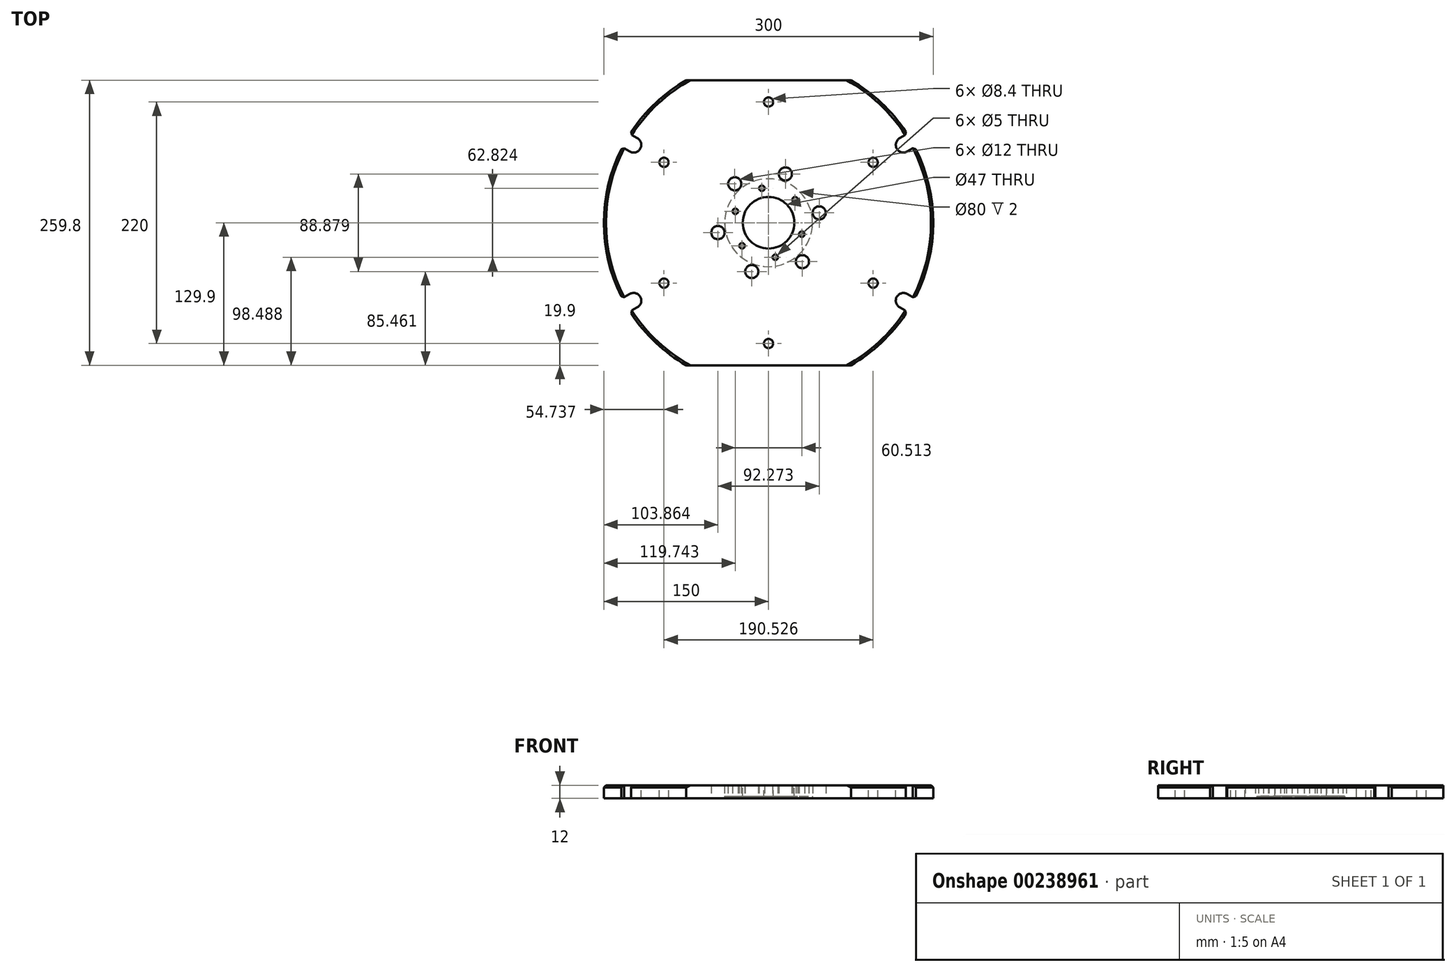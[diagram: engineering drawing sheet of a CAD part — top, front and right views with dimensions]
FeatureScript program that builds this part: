
annotation { "Feature Type Name" : "Feature", "Feature Type Description" : "" }
export const myFeature = defineFeature(function(context is Context, id is Id, definition is map)
    precondition{}
    {
        {
            var Q0;
            Q0=qCreatedBy(makeId("Top.planeOp"),FACE);
            var sketch = newSketch(context, id + "F0", { "sketchPlane" : qUnion([Q0])});
            skArc(sketch, "E0.cCircle", {"start": v(-75, 129.9) * mm, "mid": v(-103.56, 108.51) * mm, "end": v(-126.26, 80.98) * mm});
            skLineSegment(sketch, "E0.1", {"start": v(-75, 129.9) * mm, "end": v(75, 129.9) * mm});
            skLineSegment(sketch, "E0.4", {"start": v(75, -129.9) * mm, "end": v(-75, -129.9) * mm});
            skPoint(sketch, "E0.5.end.orphan", {"position": v(-150, 0) * mm});
            skCircle(sketch, "E1", {"center": v(0, 0) * mm, "radius": 110 * mm, "construction": true});
            skCircle(sketch, "E2", {"center": v(0, 110) * mm, "radius": 4.2 * mm});
            skCircle(sketch, "E3.1.0", {"center": v(-95.26, 55) * mm, "radius": 4.2 * mm});
            skCircle(sketch, "E3.2.0", {"center": v(-95.26, -55) * mm, "radius": 4.2 * mm});
            skCircle(sketch, "E3.3.0", {"center": v(0, -110) * mm, "radius": 4.2 * mm});
            skCircle(sketch, "E3.4.0", {"center": v(95.26, -55) * mm, "radius": 4.2 * mm});
            skCircle(sketch, "E3.5.0", {"center": v(95.26, 55) * mm, "radius": 4.2 * mm});
            skCircle(sketch, "E4", {"center": v(0, 0) * mm, "radius": 23.5 * mm});
            skLineSegment(sketch, "E5", {"start": v(-75, 129.9) * mm, "end": v(-150, 0) * mm, "construction": true});
            skLineSegment(sketch, "E6", {"start": v(0, 0) * mm, "end": v(-148.53, 85.75) * mm, "construction": true});
            skLineSegment(sketch, "E7", {"start": v(-110.04, 93.22) * mm, "end": v(-133.2, 53.1) * mm, "construction": true});
            skArc(sketch, "E8", {"start": v(-126.4, 64.89) * mm, "mid": v(-116.83, 67.45) * mm, "end": v(-119.4, 77.01) * mm});
            skLineSegment(sketch, "E9", {"start": v(-119.4, 77.01) * mm, "end": v(-126.26, 80.98) * mm});
            skLineSegment(sketch, "E10.MirrorCS", {"start": v(-126.4, 64.89) * mm, "end": v(-133.26, 68.86) * mm});
            skArc(sketch, "E11.trimOffspring", {"start": v(-133.26, 68.86) * mm, "mid": v(-145.76, 35.43) * mm, "end": v(-150, 0) * mm});
            skLineSegment(sketch, "E12", {"start": v(0, 0) * mm, "end": v(-185.74, 0) * mm, "construction": true});
            skLineSegment(sketch, "E13", {"start": v(0, -5.52) * mm, "end": v(0, -165.36) * mm, "construction": true});
            skArc(sketch, "E14.MirrorCS", {"start": v(-75, -129.9) * mm, "mid": v(-103.56, -108.51) * mm, "end": v(-126.26, -80.98) * mm});
            skLineSegment(sketch, "E15.MirrorCS", {"start": v(-119.4, -77.01) * mm, "end": v(-126.26, -80.98) * mm});
            skArc(sketch, "E16.MirrorCS", {"start": v(-126.4, -64.89) * mm, "mid": v(-116.83, -67.45) * mm, "end": v(-119.4, -77.01) * mm});
            skLineSegment(sketch, "E17.MirrorCS", {"start": v(-126.4, -64.89) * mm, "end": v(-133.26, -68.86) * mm});
            skArc(sketch, "E18.MirrorCS", {"start": v(-133.26, -68.86) * mm, "mid": v(-145.76, -35.43) * mm, "end": v(-150, 0) * mm});
            skArc(sketch, "E19.MirrorCS", {"start": v(75, 129.9) * mm, "mid": v(103.56, 108.51) * mm, "end": v(126.26, 80.98) * mm});
            skLineSegment(sketch, "E20.MirrorCS", {"start": v(119.4, 77.01) * mm, "end": v(126.26, 80.98) * mm});
            skArc(sketch, "E21.MirrorCS", {"start": v(126.4, 64.89) * mm, "mid": v(116.83, 67.45) * mm, "end": v(119.4, 77.01) * mm});
            skLineSegment(sketch, "E22.MirrorCS", {"start": v(126.4, 64.89) * mm, "end": v(133.26, 68.86) * mm});
            skArc(sketch, "E23.MirrorCS", {"start": v(133.26, 68.86) * mm, "mid": v(145.76, 35.43) * mm, "end": v(150, 0) * mm});
            skArc(sketch, "E24.MirrorCS", {"start": v(133.26, -68.86) * mm, "mid": v(145.76, -35.43) * mm, "end": v(150, 0) * mm});
            skLineSegment(sketch, "E25.MirrorCS", {"start": v(126.4, -64.89) * mm, "end": v(133.26, -68.86) * mm});
            skArc(sketch, "E26.MirrorCS", {"start": v(126.4, -64.89) * mm, "mid": v(116.83, -67.45) * mm, "end": v(119.4, -77.01) * mm});
            skLineSegment(sketch, "E27.MirrorCS", {"start": v(119.4, -77.01) * mm, "end": v(126.26, -80.98) * mm});
            skArc(sketch, "E28.MirrorCS", {"start": v(75, -129.9) * mm, "mid": v(103.56, -108.51) * mm, "end": v(126.26, -80.98) * mm});
            skSolve(sketch);
        }
        {
            var Q0;
            Q0=makeQuery(id+"F0.imprint","IMPRINT",FACE,{"disambiguationData":[TD([[makeQuery(id+"F0.imprint","IMPRINT",EDGE,{"derivedFrom":sQuery(id+"F0.wireOp",EDGE,"E0.cCircle")}),1.0]])]});
            extrude(context, id + "F1", {"entities" : qUnion([Q0]), "oppositeDirection" : true, "depth" : 12 * mm});
        }
        {
            var Q0;
            Q0=makeQuery(id+"F1.opExtrude","CAP_FACE",FACE,{"disambiguationData":[OSD([sQuery(id+"F0.wireOp",EDGE,"E0.cCircle"),sQuery(id+"F0.wireOp",EDGE,"E0.1"),sQuery(id+"F0.wireOp",EDGE,"E0.4"),sQuery(id+"F0.wireOp",EDGE,"4afdcd55-aeb9-484d-aa84-c3ffe76172be.trimOffspring"),sQuery(id+"F0.wireOp",EDGE,"E2"),sQuery(id+"F0.wireOp",EDGE,"E3.1.0"),sQuery(id+"F0.wireOp",EDGE,"E3.2.0"),sQuery(id+"F0.wireOp",EDGE,"E3.3.0"),sQuery(id+"F0.wireOp",EDGE,"E3.4.0"),sQuery(id+"F0.wireOp",EDGE,"E3.5.0"),sQuery(id+"F0.wireOp",EDGE,"E4")])],"isStart":false});
            cPlane(context, id + "F2", {"entities" : qUnion([Q0]), "cplaneType" : CPlaneType.OFFSET, "offset" : 0 * mm, "width" : 150 * mm, "height" : 150 * mm});
        }
        {
            var Q0;
            Q0=qCreatedBy(id+"F2.planeOp",FACE);
            var sketch = newSketch(context, id + "F3", { "sketchPlane" : qUnion([Q0])});
            skCircle(sketch, "E29", {"center": v(0, 0) * mm, "radius": 40 * mm});
            skSolve(sketch);
        }
        {
            var Q0;
            Q0 = qSketchRegion(id + "F3", true);
            extrude(context, id + "F4", {"entities" : qUnion([Q0]), "operationType" : NewBodyOperationType.REMOVE, "oppositeDirection" : true, "depth" : 2 * mm, "hasSecondDirection" : true, "secondDirectionOppositeDirection" : false, "secondDirectionDepth" : 10 * mm});
        }
        {
            var Q0;
            Q0=qCreatedBy(id+"F2.planeOp",FACE);
            var sketch = newSketch(context, id + "F5", { "sketchPlane" : qUnion([Q0])});
            skCircle(sketch, "E30", {"center": v(0, 0) * mm, "radius": 32 * mm, "construction": true});
            skLineSegment(sketch, "E31", {"start": v(0, 0) * mm, "end": v(8.68, 44.64) * mm, "construction": true});
            skPoint(sketch, "E32", {"position": v(6.1, 31.41) * mm});
            skPoint(sketch, "E33.1.0", {"position": v(-24.15, 21) * mm});
            skPoint(sketch, "E33.2.0", {"position": v(-30.26, -10.42) * mm});
            skPoint(sketch, "E33.3.0", {"position": v(-6.1, -31.41) * mm});
            skPoint(sketch, "E33.4.0", {"position": v(24.15, -21) * mm});
            skPoint(sketch, "E33.5.0", {"position": v(30.26, 10.42) * mm});
            skCircle(sketch, "E34", {"center": v(0, 0) * mm, "radius": 55 * mm, "construction": true});
            skCircle(sketch, "E35", {"center": v(0, 0) * mm, "radius": 47 * mm, "construction": true});
            skLineSegment(sketch, "E36", {"start": v(0, 0) * mm, "end": v(-26.12, 75.86) * mm, "construction": true});
            skPoint(sketch, "E37", {"position": v(-15.3, 44.44) * mm});
            skPoint(sketch, "E38.1.0", {"position": v(-46.14, 8.97) * mm});
            skPoint(sketch, "E38.2.0", {"position": v(-30.83, -35.47) * mm});
            skPoint(sketch, "E38.3.0", {"position": v(15.3, -44.44) * mm});
            skPoint(sketch, "E38.4.0", {"position": v(46.14, -8.97) * mm});
            skPoint(sketch, "E38.5.0", {"position": v(30.83, 35.47) * mm});
            skSolve(sketch);
        }
        {
            var Q0;
            Q0=sQuery(id+"F5.wireOp",VERTEX,"E32");
            var Q1;
            Q1=sQuery(id+"F5.wireOp",VERTEX,"E33.1.0");
            var Q2;
            Q2=sQuery(id+"F5.wireOp",VERTEX,"E33.2.0");
            var Q3;
            Q3=sQuery(id+"F5.wireOp",VERTEX,"E33.3.0");
            var Q4;
            Q4=sQuery(id+"F5.wireOp",VERTEX,"E33.4.0");
            var Q5;
            Q5=sQuery(id+"F5.wireOp",VERTEX,"E33.5.0");
            var Q6;
            Q6=makeQuery(id+"F1.opExtrude","SWEPT_BODY",BODY,{"disambiguationData":[OSD([sQuery(id+"F0.wireOp",EDGE,"E0.cCircle"),sQuery(id+"F0.wireOp",EDGE,"E0.1"),sQuery(id+"F0.wireOp",EDGE,"E0.4"),sQuery(id+"F0.wireOp",EDGE,"4afdcd55-aeb9-484d-aa84-c3ffe76172be.trimOffspring"),sQuery(id+"F0.wireOp",EDGE,"E2"),sQuery(id+"F0.wireOp",EDGE,"E3.1.0"),sQuery(id+"F0.wireOp",EDGE,"E3.2.0"),sQuery(id+"F0.wireOp",EDGE,"E3.3.0"),sQuery(id+"F0.wireOp",EDGE,"E3.4.0"),sQuery(id+"F0.wireOp",EDGE,"E3.5.0"),sQuery(id+"F0.wireOp",EDGE,"E4")])]});
            hole(context, id + "F6", {"style" : HoleStyle.SIMPLE, "endStyle" : HoleEndStyle.THROUGH, "holeDiameter" : 5 * mm, "locations" : qUnion([Q0, Q1, Q2, Q3, Q4, Q5]), "scope" : qUnion([Q6]), "isTappedThrough" : true});
        }
        {
            var Q0;
            Q0=sQuery(id+"F5.wireOp",VERTEX,"E38.2.0");
            var Q1;
            Q1=sQuery(id+"F5.wireOp",VERTEX,"E38.3.0");
            var Q2;
            Q2=sQuery(id+"F5.wireOp",VERTEX,"E38.4.0");
            var Q3;
            Q3=sQuery(id+"F5.wireOp",VERTEX,"E38.5.0");
            var Q4;
            Q4=sQuery(id+"F5.wireOp",VERTEX,"E37");
            var Q5;
            Q5=sQuery(id+"F5.wireOp",VERTEX,"E38.1.0");
            var Q6;
            Q6=makeQuery(id+"F1.opExtrude","SWEPT_BODY",BODY,{"disambiguationData":[OSD([sQuery(id+"F0.wireOp",EDGE,"E0.cCircle"),sQuery(id+"F0.wireOp",EDGE,"E0.1"),sQuery(id+"F0.wireOp",EDGE,"E0.4"),sQuery(id+"F0.wireOp",EDGE,"4afdcd55-aeb9-484d-aa84-c3ffe76172be.trimOffspring"),sQuery(id+"F0.wireOp",EDGE,"E2"),sQuery(id+"F0.wireOp",EDGE,"E3.1.0"),sQuery(id+"F0.wireOp",EDGE,"E3.2.0"),sQuery(id+"F0.wireOp",EDGE,"E3.3.0"),sQuery(id+"F0.wireOp",EDGE,"E3.4.0"),sQuery(id+"F0.wireOp",EDGE,"E3.5.0"),sQuery(id+"F0.wireOp",EDGE,"E4")])]});
            hole(context, id + "F7", {"style" : HoleStyle.SIMPLE, "endStyle" : HoleEndStyle.THROUGH, "holeDiameter" : 12 * mm, "locations" : qUnion([Q0, Q1, Q2, Q3, Q4, Q5]), "scope" : qUnion([Q6]), "isTappedThrough" : true});
        }
        {
            var Q0;
            Q0=makeQuery(id+"F1.opExtrude","SWEPT_EDGE",EDGE,{"disambiguationData":[OSD([sQuery(id+"F0.wireOp",EDGE,"E27.MirrorCS"),sQuery(id+"F0.wireOp",EDGE,"E28.MirrorCS")])]});
            var Q1;
            Q1=makeQuery(id+"F1.opExtrude","SWEPT_EDGE",EDGE,{"disambiguationData":[OSD([sQuery(id+"F0.wireOp",EDGE,"E24.MirrorCS"),sQuery(id+"F0.wireOp",EDGE,"E25.MirrorCS")])]});
            var Q2;
            Q2=makeQuery(id+"F1.opExtrude","SWEPT_EDGE",EDGE,{"disambiguationData":[OSD([sQuery(id+"F0.wireOp",EDGE,"E22.MirrorCS"),sQuery(id+"F0.wireOp",EDGE,"E23.MirrorCS")])]});
            var Q3;
            Q3=makeQuery(id+"F1.opExtrude","SWEPT_EDGE",EDGE,{"disambiguationData":[OSD([sQuery(id+"F0.wireOp",EDGE,"E19.MirrorCS"),sQuery(id+"F0.wireOp",EDGE,"E20.MirrorCS")])]});
            var Q4;
            Q4=makeQuery(id+"F1.opExtrude","SWEPT_EDGE",EDGE,{"disambiguationData":[OSD([sQuery(id+"F0.wireOp",EDGE,"E0.cCircle"),sQuery(id+"F0.wireOp",EDGE,"E9")])]});
            var Q5;
            Q5=makeQuery(id+"F1.opExtrude","SWEPT_EDGE",EDGE,{"disambiguationData":[OSD([sQuery(id+"F0.wireOp",EDGE,"E10.MirrorCS"),sQuery(id+"F0.wireOp",EDGE,"E11.trimOffspring")])]});
            var Q6;
            Q6=makeQuery(id+"F1.opExtrude","SWEPT_EDGE",EDGE,{"disambiguationData":[OSD([sQuery(id+"F0.wireOp",EDGE,"E17.MirrorCS"),sQuery(id+"F0.wireOp",EDGE,"E18.MirrorCS")])]});
            var Q7;
            Q7=makeQuery(id+"F1.opExtrude","SWEPT_EDGE",EDGE,{"disambiguationData":[OSD([sQuery(id+"F0.wireOp",EDGE,"E14.MirrorCS"),sQuery(id+"F0.wireOp",EDGE,"E15.MirrorCS")])]});
            chamfer(context, id + "F8", {"entities" : qUnion([Q0, Q1, Q2, Q3, Q4, Q5, Q6, Q7]), "width" : 2 * mm, "tangentPropagation" : true});
        }
        {
            var Q0;
            Q0=makeQuery(id+"F1.opExtrude","CAP_EDGE",EDGE,{"disambiguationData":[OSD([sQuery(id+"F0.wireOp",EDGE,"E28.MirrorCS")])],"isStart":true});
            var Q1;
            Q1=makeQuery(id+"F1.opExtrude","CAP_EDGE",EDGE,{"disambiguationData":[OSD([sQuery(id+"F0.wireOp",EDGE,"E23.MirrorCS"),sQuery(id+"F0.wireOp",EDGE,"E24.MirrorCS")])],"isStart":true});
            var Q2;
            Q2=makeQuery(id+"F1.opExtrude","CAP_EDGE",EDGE,{"disambiguationData":[OSD([sQuery(id+"F0.wireOp",EDGE,"E19.MirrorCS")])],"isStart":true});
            var Q3;
            Q3=makeQuery(id+"F1.opExtrude","CAP_EDGE",EDGE,{"disambiguationData":[OSD([sQuery(id+"F0.wireOp",EDGE,"E0.cCircle")])],"isStart":true});
            var Q4;
            Q4=makeQuery(id+"F1.opExtrude","CAP_EDGE",EDGE,{"disambiguationData":[OSD([sQuery(id+"F0.wireOp",EDGE,"E11.trimOffspring"),sQuery(id+"F0.wireOp",EDGE,"E18.MirrorCS")])],"isStart":true});
            var Q5;
            Q5=makeQuery(id+"F1.opExtrude","CAP_EDGE",EDGE,{"disambiguationData":[OSD([sQuery(id+"F0.wireOp",EDGE,"E14.MirrorCS")])],"isStart":true});
            chamfer(context, id + "F9", {"entities" : qUnion([Q0, Q1, Q2, Q3, Q4, Q5]), "width" : 2 * mm, "tangentPropagation" : true});
        }
    });
